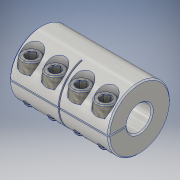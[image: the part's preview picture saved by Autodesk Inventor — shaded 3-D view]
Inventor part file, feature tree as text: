
AUTODESK INVENTOR PART (.ipt)
format: ipt  version: 2016 (Build 200138000, 138)  size: 1,904,640 bytes
history: native  units: in
note: dims shown in document units (in); Inventor stores cm internally (conversion verified against a paired STEP export)
features: other x4, mirror x1
ambient origin geometry x8: Origin, YZ Plane, XZ Plane, XY Plane, X Axis, Y Axis, Z Axis, Center Point
bodies: Solid1 (feature_tree), Solid2 (feature_tree), Solid3 (feature_tree), Solid4 (feature_tree), Solid5 (feature_tree)
feature tree (5):
  other  "Cut-Sweep1"
  mirror  "Mirror1"
  other  "LPattern2"
  other  "LPattern3[1]"
  other  "LPattern3[2]"
